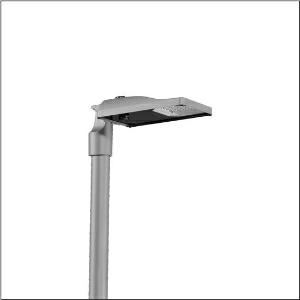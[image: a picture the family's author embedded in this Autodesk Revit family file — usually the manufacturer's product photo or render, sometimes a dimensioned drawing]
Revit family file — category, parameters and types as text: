
# Revit family: streetlight_sl_31_micro___st0_5a_5xh5b31t08da_db8b
name_source: partatom
category: Lighting Fixtures
units: mm (PartAtom-declared; Revit-internal decimal feet)

## family parameters
Cut with Voids When Loaded = No
Host = Face
Light Source = No
Part Type = Normal
Room Calculation Point = No
Round Connector Dimension = Use Diameter
Shared = No

## types (1)
- --- (1 x LED, 4940 lm, 37.7 W, 3000K)
    Apparent Load = 38 VA
    CIE Flux Codes = 41 75 97 100 100
    Color Rendering = 70
    Color Temperature = 3000K
    Default Elevation = 1800 mm
    Description = Streetlight SL 31 micro D4i, Desk-Remote mast luminaire for post-top, side-entry; light control with lens of PMMA; light distribution: ST0.5a, direct asymmetric distribution, for standard-compliant lighting for roads and squares; LED: luminous flux: 4.940lm, light colour: 730, colour temperature: 3000K; luminous efficacy: 131lm/W; control: pre-setting: logarithmic dimming characteristic, flexible luminous flux parameterisation, time-dependent luminous flux control, constant luminous flux control, power reduction, intelligent temperature release in ECG and LED module, overheat protection; luminaire housing, of diecast aluminium, Siteco® metallic grey (DB 702S), corrosivity category C5 high according to DIN EN ISO 12944; cover of toughened safety glass, transparent, opened without tools; mast flange of diecast aluminium, Siteco® metallic grey (DB 702S), spigot size: 76/60mm, mast flange included unmounted; with cable H07RN-F 2x 1.5mm², cable length: 6,5m, connection cable pre-assembled; mains connection: 220..240V, AC, 50/60Hz; power consumption (at start of service life): 37,7W / (at end of service life): 40,9W / (with reduced operation 50%): 16,3W; protection rating (complete): IP66; insulation class (complete): insulation class II (safety insulation); impact resistance: IK09; certification: CE, ENEC, ENEC+, VDE, UKCA, ZD4i; permissible operating ambient temperature for outdoor applications: -40..+50°C; packaging unit: 1 piece

Light Distribution: ST0.5a
    Height = 76 mm
    Lamp = 1 x LED
    Lamp Light Flux = 4940 lm
    Lamp Power = 37.7 W
    Lamp count = 1
    Length = 467 mm
    Luminous efficacy = 131 lm/W
    Manufacturer = Siteco
    ModVariant = No
    Model = 5XH5B31T08DA
    Number of Poles = 1
    OnlyDefault = Yes
    Power Factor = 1
    Product Name = Streetlight SL 31 micro | ST0.5a
    Product group = mast luminaire | pylon top
    ProductGroupID = 6100
    Protection Class = Protection class II
    Protection Degree = IP 66
    RLX_Detail_Level = 1
    RLX_Emergency_Light_Flux = 0 lm
    RLX_Emergency_Type = 0
    RLX_Emergency_Type_DB = No
    RlxData = <blob elided: 55073 chars, md5=06bcf43a>
    Socket = socket
    Standby Power = 0 W
    System Light Flux = 4940 lm
    System Power = 38 W
    Type Comments = factory setting: luminous flux: 100 % | dim-lin: 254 | 745 mA
    Type Image = l_1300315.jpg
    URL = http://relux.com
    VarID = @adj_015107
    Voltage = 0 V
    Weight = 0.00 kg
    Width = 265 mm

## geometry (parser evidence)
native form markers: Blend x4, Sweep x11
no freeform markers — native parametric forms only
